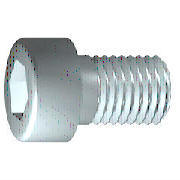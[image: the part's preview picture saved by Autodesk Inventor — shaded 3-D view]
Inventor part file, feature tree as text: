
AUTODESK INVENTOR PART (.ipt)
format: ipt  version: 2023.3 (Build 273359000, 359)  size: 185,856 bytes
history: native  units: mm (DEFAULTED — no unit token found)
features: sketch x2, other x1, extrude x1, plane x1, fillet x1
ambient origin geometry x7: Origin, YZ Plane, XY Plane, X Axis, Y Axis, Z Axis, Center Point
bodies: Solid1 (feature_tree)
feature tree (6):
  other  "Körper"
  extrude  "Loch"  Depth=3.0mm
  plane  "Work Plane1"
  fillet  "Fillet2"  Radius=3.0mm
  sketch  "Skizze1"  dims[d1=18.0mm d2=0.306825mm d3=3.0mm]
  sketch  "Skizze2"  dims[d4=1.3mm d5=60.0deg d6=3.0mm d7=3.0mm d8=2.886751mm d9=5.5mm d10=90.0deg d11=10.0mm d12=0.0mm d13=18.0mm d14=0.0mm d15=0.306725mm d16=0.306725mm d17=0.3mm d19=0.0mm d26=30.0mm d27=45.0deg d28=0.0mm d29=0.0mm d30=0.1mm]
